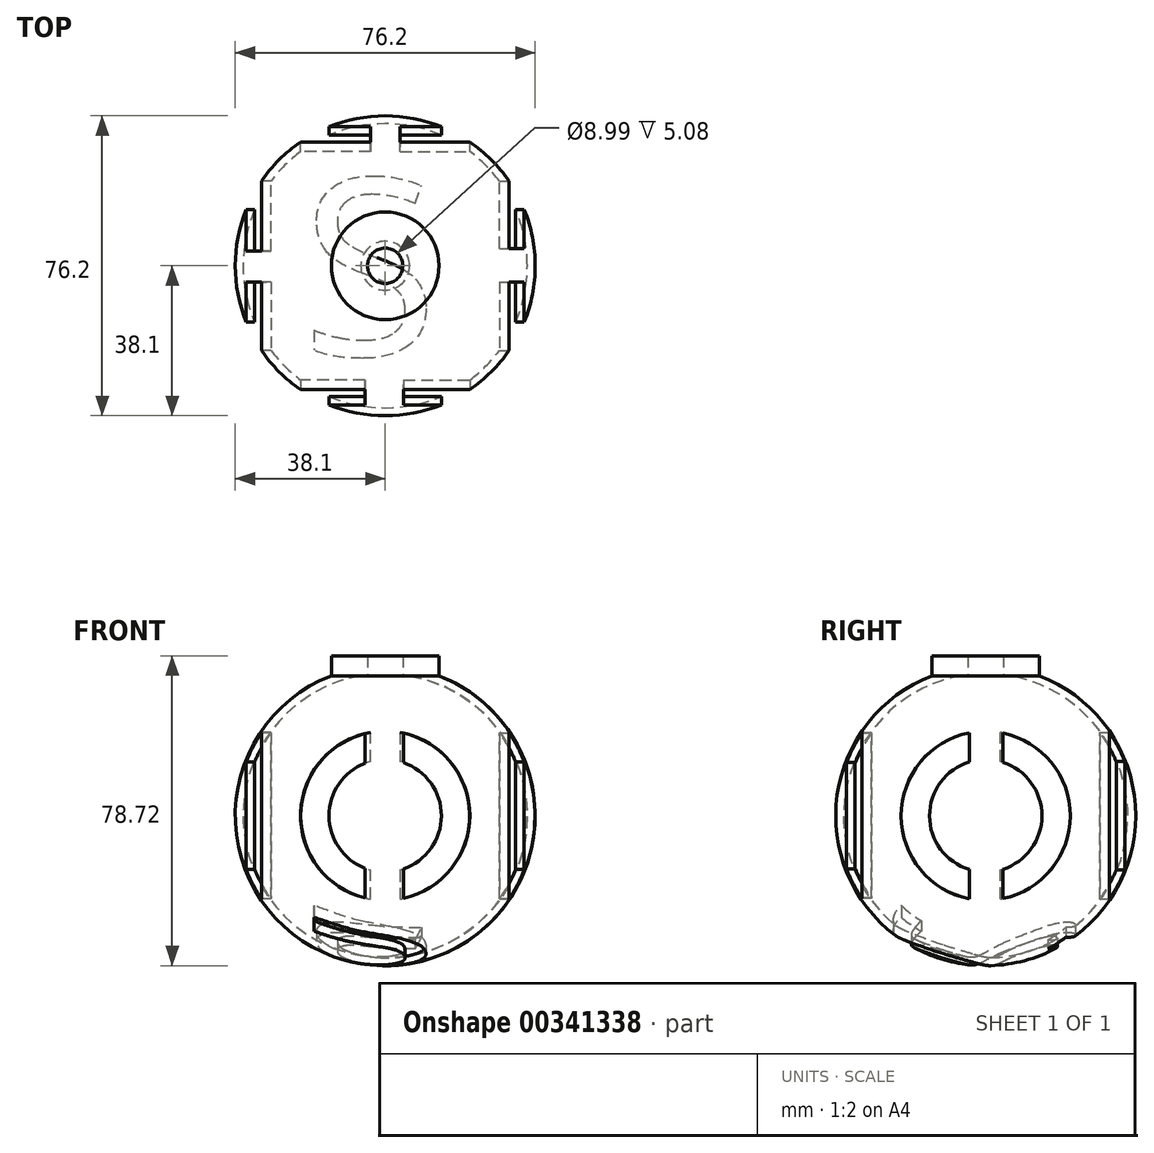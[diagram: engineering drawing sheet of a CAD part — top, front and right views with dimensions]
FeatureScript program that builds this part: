
annotation { "Feature Type Name" : "Feature", "Feature Type Description" : "" }
export const myFeature = defineFeature(function(context is Context, id is Id, definition is map)
    precondition{}
    {
        {
            var Q0;
            Q0=qCreatedBy(makeId("Front.planeOp"),FACE);
            var sketch = newSketch(context, id + "F0", { "sketchPlane" : qUnion([Q0])});
            skArc(sketch, "E0", {"start": v(0, -38.1) * mm, "mid": v(38.1, 0) * mm, "end": v(0, 38.1) * mm});
            skLineSegment(sketch, "E1", {"start": v(0, -38.1) * mm, "end": v(0, 38.1) * mm});
            skSolve(sketch);
        }
        {
            var Q0;
            Q0=makeQuery(id+"F0.imprint","IMPRINT",FACE,{"disambiguationData":[TD([[makeQuery(id+"F0.imprint","IMPRINT",EDGE,{"derivedFrom":sQuery(id+"F0.wireOp",EDGE,"E0")}),1.0]])]});
            var Q1;
            Q1=sQuery(id+"F0.wireOp",EDGE,"E1");
            revolve(context, id + "F1", {"entities" : qUnion([Q0]), "axis" : qUnion([Q1]), "revolveType" : RevolveType.FULL});
        }
        {
            var Q0;
            Q0=qCreatedBy(makeId("Top.planeOp"),FACE);
            cPlane(context, id + "F2", {"entities" : qUnion([Q0]), "cplaneType" : CPlaneType.OFFSET, "offset" : 35.56 * mm, "width" : 152.4 * mm, "height" : 152.4 * mm});
        }
        {
            var Q0;
            Q0=qCreatedBy(id+"F2.planeOp",FACE);
            var sketch = newSketch(context, id + "F3", { "sketchPlane" : qUnion([Q0])});
            skLineSegment(sketch, "E2.bottom", {"start": v(16.51, 16.51) * mm, "end": v(-16.51, 16.51) * mm});
            skLineSegment(sketch, "E2.top", {"start": v(16.51, -16.51) * mm, "end": v(-16.51, -16.51) * mm});
            skLineSegment(sketch, "E2.left", {"start": v(16.51, 16.51) * mm, "end": v(16.51, -16.51) * mm});
            skLineSegment(sketch, "E2.right", {"start": v(-16.51, 16.51) * mm, "end": v(-16.51, -16.51) * mm});
            skPoint(sketch, "E2.middle", {"position": v(0, 0) * mm});
            skSolve(sketch);
        }
        {
            var Q0;
            Q0=makeQuery(id+"F3.imprint","IMPRINT",FACE,{"disambiguationData":[TD([[makeQuery(id+"F3.imprint","IMPRINT",EDGE,{"derivedFrom":sQuery(id+"F3.wireOp",EDGE,"E2.bottom")}),1.0]])]});
            extrude(context, id + "F4", {"entities" : qUnion([Q0]), "operationType" : NewBodyOperationType.REMOVE, "depth" : 25.4 * mm});
        }
        {
            var Q0;
            Q0=makeQuery(id+"F4.boolean.opBoolean","COPY",FACE,{"derivedFrom":makeQuery(id+"F4.opExtrude","CAP_FACE",FACE,{"disambiguationData":[OSD([sQuery(id+"F3.wireOp",EDGE,"E2.bottom"),sQuery(id+"F3.wireOp",EDGE,"E2.top"),sQuery(id+"F3.wireOp",EDGE,"E2.left"),sQuery(id+"F3.wireOp",EDGE,"E2.right")])],"isStart":true})});
            shell(context, id + "F5", {"entities" : qUnion([Q0]), "thickness" : 2 * mm});
        }
        {
            var Q0;
            Q0=qCreatedBy(makeId("Right.planeOp"),FACE);
            cPlane(context, id + "F6", {"entities" : qUnion([Q0]), "cplaneType" : CPlaneType.OFFSET, "offset" : 38.1 * mm, "width" : 152.4 * mm, "height" : 152.4 * mm});
        }
        {
            var Q0;
            Q0=qCreatedBy(id+"F6.planeOp",FACE);
            var sketch = newSketch(context, id + "F7", { "sketchPlane" : qUnion([Q0])});
            skArc(sketch, "E3", {"start": v(-4.12, 21.1) * mm, "mid": v(-21.5, 0) * mm, "end": v(-4.12, -21.1) * mm});
            skArc(sketch, "E4", {"start": v(-4.12, 13.67) * mm, "mid": v(-14.27, 0) * mm, "end": v(-4.12, -13.67) * mm});
            skLineSegment(sketch, "E5", {"start": v(-4.12, 13.67) * mm, "end": v(-4.12, 21.1) * mm});
            skLineSegment(sketch, "E6", {"start": v(4.38, 13.58) * mm, "end": v(4.38, 21.04) * mm});
            skLineSegment(sketch, "E7", {"start": v(4.38, -13.58) * mm, "end": v(4.38, -21.04) * mm});
            skLineSegment(sketch, "E8", {"start": v(-4.12, -13.67) * mm, "end": v(-4.12, -21.1) * mm});
            skArc(sketch, "E9.trimOffspring", {"start": v(4.38, -13.58) * mm, "mid": v(14.27, 0) * mm, "end": v(4.38, 13.58) * mm});
            skArc(sketch, "E10.trimOffspring", {"start": v(4.38, -21.04) * mm, "mid": v(21.5, 0) * mm, "end": v(4.38, 21.04) * mm});
            skSolve(sketch);
        }
        {
            var Q0;
            Q0=makeQuery(id+"F7.imprint","IMPRINT",FACE,{"disambiguationData":[TD([[makeQuery(id+"F7.imprint","IMPRINT",EDGE,{"derivedFrom":sQuery(id+"F7.wireOp",EDGE,"E3")}),1.0]])]});
            extrude(context, id + "F8", {"entities" : qUnion([Q0]), "operationType" : NewBodyOperationType.REMOVE, "oppositeDirection" : true, "depth" : 25.4 * mm});
        }
        {
            var Q0;
            Q0=makeQuery(id+"F7.imprint","IMPRINT",FACE,{"disambiguationData":[TD([[makeQuery(id+"F7.imprint","IMPRINT",EDGE,{"derivedFrom":sQuery(id+"F7.wireOp",EDGE,"E6")}),-1.0]])]});
            extrude(context, id + "F9", {"entities" : qUnion([Q0]), "operationType" : NewBodyOperationType.REMOVE, "oppositeDirection" : true, "depth" : 25.4 * mm});
        }
        {
            var Q0;
            Q0=qCreatedBy(makeId("Front.planeOp"),FACE);
            cPlane(context, id + "F10", {"entities" : qUnion([Q0]), "cplaneType" : CPlaneType.OFFSET, "offset" : 38.1 * mm, "oppositeDirection" : true, "width" : 152.4 * mm, "height" : 152.4 * mm});
        }
        {
            var Q0;
            Q0=qCreatedBy(id+"F10.planeOp",FACE);
            var sketch = newSketch(context, id + "F11", { "sketchPlane" : qUnion([Q0])});
            skArc(sketch, "E11", {"start": v(-3.67, 21.17) * mm, "mid": v(-21.49, 0) * mm, "end": v(-3.67, -21.17) * mm});
            skArc(sketch, "E12", {"start": v(-3.67, 13.8) * mm, "mid": v(-14.27, 0) * mm, "end": v(-3.67, -13.8) * mm});
            skLineSegment(sketch, "E13", {"start": v(-3.67, 21.17) * mm, "end": v(-3.67, 13.8) * mm});
            skLineSegment(sketch, "E14", {"start": v(3.78, -21.15) * mm, "end": v(3.78, -13.77) * mm});
            skLineSegment(sketch, "E15.trimOffspring", {"start": v(3.78, 13.77) * mm, "end": v(3.78, 21.15) * mm});
            skLineSegment(sketch, "E16.trimOffspring", {"start": v(-3.67, -13.8) * mm, "end": v(-3.67, -21.17) * mm});
            skArc(sketch, "E17.trimOffspring", {"start": v(3.78, -13.77) * mm, "mid": v(14.27, 0) * mm, "end": v(3.78, 13.77) * mm});
            skArc(sketch, "E18.trimOffspring", {"start": v(3.78, -21.15) * mm, "mid": v(21.49, 0) * mm, "end": v(3.78, 21.15) * mm});
            skSolve(sketch);
        }
        {
            var Q0;
            Q0 = qSketchRegion(id + "F11", true);
            extrude(context, id + "F12", {"entities" : qUnion([Q0]), "operationType" : NewBodyOperationType.REMOVE, "depth" : 25.4 * mm});
        }
        {
            var Q0;
            Q0=qCreatedBy(makeId("Right.planeOp"),FACE);
            cPlane(context, id + "F13", {"entities" : qUnion([Q0]), "cplaneType" : CPlaneType.OFFSET, "offset" : 38.1 * mm, "oppositeDirection" : true, "width" : 152.4 * mm, "height" : 152.4 * mm});
        }
        {
            var Q0;
            Q0=qCreatedBy(id+"F13.planeOp",FACE);
            var sketch = newSketch(context, id + "F14", { "sketchPlane" : qUnion([Q0])});
            skArc(sketch, "E19", {"start": v(-4.13, 13.66) * mm, "mid": v(-14.27, 0) * mm, "end": v(-4.13, -13.66) * mm});
            skArc(sketch, "E20", {"start": v(-4.13, 21.09) * mm, "mid": v(-21.49, 0) * mm, "end": v(-4.13, -21.09) * mm});
            skLineSegment(sketch, "E21", {"start": v(-4.13, -21.09) * mm, "end": v(-4.13, -13.66) * mm});
            skLineSegment(sketch, "E22", {"start": v(3.75, 21.16) * mm, "end": v(3.75, 13.77) * mm});
            skLineSegment(sketch, "E23.trimOffspring", {"start": v(3.75, -13.77) * mm, "end": v(3.75, -21.16) * mm});
            skLineSegment(sketch, "E24.trimOffspring", {"start": v(-4.13, 13.66) * mm, "end": v(-4.13, 21.09) * mm});
            skArc(sketch, "E25.trimOffspring", {"start": v(3.75, -13.77) * mm, "mid": v(14.27, 0) * mm, "end": v(3.75, 13.77) * mm});
            skArc(sketch, "E26.trimOffspring", {"start": v(3.75, -21.16) * mm, "mid": v(21.49, 0) * mm, "end": v(3.75, 21.16) * mm});
            skSolve(sketch);
        }
        {
            var Q0;
            Q0 = qSketchRegion(id + "F14", true);
            extrude(context, id + "F15", {"entities" : qUnion([Q0]), "operationType" : NewBodyOperationType.REMOVE, "depth" : 25.4 * mm});
        }
        {
            var Q0;
            Q0=qCreatedBy(makeId("Front.planeOp"),FACE);
            cPlane(context, id + "F16", {"entities" : qUnion([Q0]), "cplaneType" : CPlaneType.OFFSET, "offset" : 38.1 * mm, "width" : 152.4 * mm, "height" : 152.4 * mm});
        }
        {
            var Q0;
            Q0=qCreatedBy(id+"F16.planeOp",FACE);
            var sketch = newSketch(context, id + "F17", { "sketchPlane" : qUnion([Q0])});
            skArc(sketch, "E27", {"start": v(-5.1, 13.33) * mm, "mid": v(-14.27, 0) * mm, "end": v(-5.1, -13.33) * mm});
            skArc(sketch, "E28", {"start": v(-5.1, 20.87) * mm, "mid": v(-21.49, 0) * mm, "end": v(-5.1, -20.87) * mm});
            skLineSegment(sketch, "E29", {"start": v(4.6, -21) * mm, "end": v(4.6, -13.51) * mm});
            skLineSegment(sketch, "E30", {"start": v(-5.1, 20.87) * mm, "end": v(-5.1, 13.33) * mm});
            skArc(sketch, "E31.trimOffspring", {"start": v(4.6, -13.51) * mm, "mid": v(14.27, 0) * mm, "end": v(4.6, 13.51) * mm});
            skArc(sketch, "E32.trimOffspring", {"start": v(4.6, -21) * mm, "mid": v(21.49, 0) * mm, "end": v(4.6, 21) * mm});
            skLineSegment(sketch, "E33.trimOffspring", {"start": v(-5.1, -13.33) * mm, "end": v(-5.1, -20.87) * mm});
            skLineSegment(sketch, "E34.trimOffspring", {"start": v(4.6, 13.51) * mm, "end": v(4.6, 21) * mm});
            skSolve(sketch);
        }
        {
            var Q0;
            Q0 = qSketchRegion(id + "F17", true);
            extrude(context, id + "F18", {"entities" : qUnion([Q0]), "operationType" : NewBodyOperationType.REMOVE, "oppositeDirection" : true, "depth" : 25.4 * mm});
        }
        {
            var Q0;
            Q0=qCreatedBy(makeId("Top.planeOp"),FACE);
            cPlane(context, id + "F19", {"entities" : qUnion([Q0]), "cplaneType" : CPlaneType.OFFSET, "offset" : 38.1 * mm, "oppositeDirection" : true, "width" : 152.4 * mm, "height" : 152.4 * mm});
        }
        {
            var Q0;
            Q0=qCreatedBy(id+"F19.planeOp",FACE);
            var sketch = newSketch(context, id + "F20", { "sketchPlane" : qUnion([Q0])});
            skText(sketch, "E35", { "text": "S", "fontName": "OpenSans-Regular.ttf"});
            const initialGuessF20  = {"E35": [-0.02128, -0.02288, 1, 0, 0.04547]};
            skSetInitialGuess(sketch, initialGuessF20);
            skSolve(sketch);
        }
        {
            var Q0;
            Q0=makeQuery(id+"F20.imprint","IMPRINT",FACE,{"disambiguationData":[TD([[makeQuery(id+"F20.imprint","IMPRINT",EDGE,{"derivedFrom":sQuery(id+"F20.wireOp",EDGE,"E35.sketch_text.stroke-0")}),-1.0]])]});
            extrude(context, id + "F21", {"entities" : qUnion([Q0]), "operationType" : NewBodyOperationType.REMOVE, "depth" : 25.4 * mm});
        }
        {
            var Q0;
            Q0=makeQuery(id+"F4.boolean.opBoolean","COPY",FACE,{"derivedFrom":makeQuery(id+"F4.opExtrude","CAP_FACE",FACE,{"disambiguationData":[OSD([sQuery(id+"F3.wireOp",EDGE,"E2.bottom"),sQuery(id+"F3.wireOp",EDGE,"E2.top"),sQuery(id+"F3.wireOp",EDGE,"E2.left"),sQuery(id+"F3.wireOp",EDGE,"E2.right")])],"isStart":true})});
            var sketch = newSketch(context, id + "F22", { "sketchPlane" : qUnion([Q0])});
            skCircle(sketch, "E36", {"center": v(0, 0) * mm, "radius": 4.5 * mm});
            skSolve(sketch);
        }
        {
            var Q0;
            {var subQ0=sQuery(id+"F3.wireOp",EDGE,"E2.right");var subQ1=sQuery(id+"F3.wireOp",EDGE,"E2.left");var subQ2=sQuery(id+"F3.wireOp",EDGE,"E2.top");var subQ3=sQuery(id+"F3.wireOp",EDGE,"E2.bottom");var subQ4=sQuery(id+"F0.wireOp",EDGE,"E0");Q0=makeQuery(id+"F22.imprint","IMPRINT",FACE,{"disambiguationData":[TD([[makeQuery(id+"F22.imprint","IMPRINT",EDGE,{"derivedFrom":makeQuery(id+"F4.boolean.opBoolean","INTERSECT",EDGE,{"derivedFrom":[makeQuery(id+"F1.opRevolve","SWEPT_FACE",FACE,{"disambiguationData":[OSD([subQ4])]}),makeQuery(id+"F4.opExtrude","CAP_FACE",FACE,{"disambiguationData":[OSD([subQ3,subQ2,subQ1,subQ0])],"isStart":true})]})}),-1.0]])]});}
            var Q1;
            Q1=makeQuery(id+"F22.imprint","IMPRINT",FACE,{"disambiguationData":[TD([[makeQuery(id+"F22.imprint","IMPRINT",EDGE,{"derivedFrom":sQuery(id+"F22.wireOp",EDGE,"E36")}),-1.0]])]});
            extrude(context, id + "F23", {"entities" : qUnion([Q0, Q1]), "operationType" : NewBodyOperationType.ADD, "depth" : 5.08 * mm});
        }
    });
